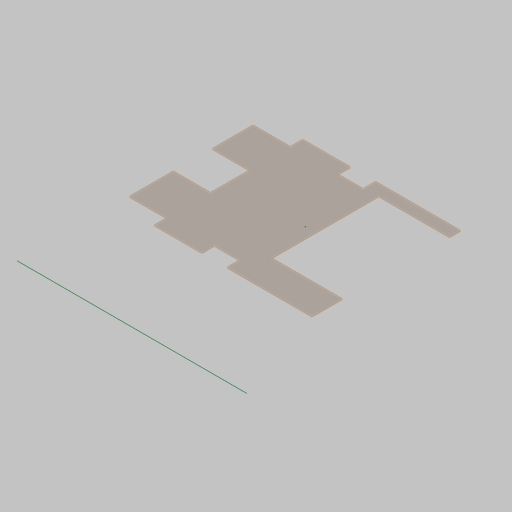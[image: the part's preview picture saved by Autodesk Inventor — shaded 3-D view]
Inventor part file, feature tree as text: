
AUTODESK INVENTOR PART (.ipt)
format: ipt  version: 2023.5 (Build 275446000, 446)  size: 259,584 bytes
history: native  units: in
note: dims shown in document units (in); Inventor stores cm internally (conversion verified against a paired STEP export)
features: sketch x5, other x3, projected_geometry x3, sheet_metal_op x1, extrude x1
ambient origin geometry x8: Origin, YZ Plane, XZ Plane, XY Plane, X Axis, Y Axis, Z Axis, Center Point
bodies: Solid1 (feature_tree)
feature tree (13):
  sheet_metal_op  "Face1"
  sketch  "Sketch3"  dims[d2=0.12in]
  extrude  "Extrusion1"  Depth=28.0in
  sketch  "Sketch1"  dims[d0=18.5in d1=28.0in]
  other  "Plate1"
  sketch  "Sketch4"  dims[d3=8.25in]
  projected_geometry  "Projected Loop1"
  sketch  "Sketch5"  dims[d4=10.0in]
  sketch  "Sketch6"  dims[d5=45.0deg d6=2.4in d9=2.75in d10=0.12in d11=0.0in d12=45.0deg d13=8.25in d14=9.0in d15=2.75in d16=2.4in d17=6.75in d18=4.5in d19=0.25in d21=4.0in d22=1.0in d23=0.1in d26=5.7in d31=0.5in d32=4.5in d33=6.75in d34=0.25in d35=4.0in d36=1.0in d37=0.1in d38=3.0in d39=1.4in d40=1.7in d41=0.1in d42=1.0in d43=0.75in d44=1.0in d45=0.75in d46=0.75in d47=1.0in d48=0.75in d49=1.0in d50=0.12in d51=0.0in d52=1.75in d53=1.0in d54=3.5in d55=1.75in d56=1.0in d57=3.5in d58=1.0in d59=0.125in d60=3.0in d61=2.0in d62=11.0in d63=1.0in d64=0.0in]
  other  "Cut1"
  other  "Cut2"
  projected_geometry  "Project Cut Edges1"
  projected_geometry  "Project Cut Edges2"
